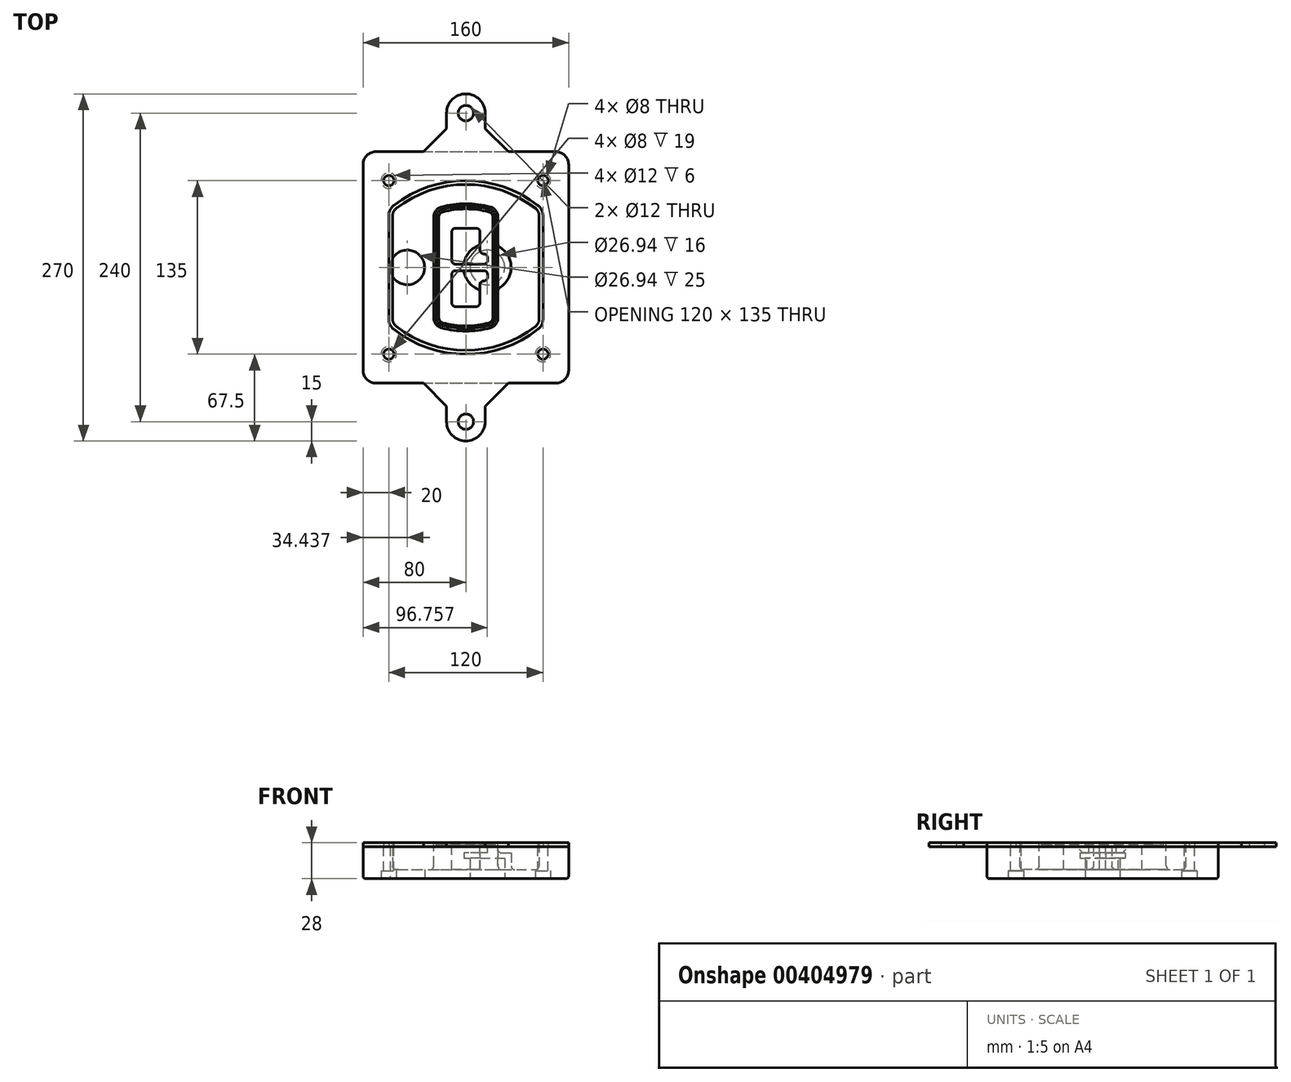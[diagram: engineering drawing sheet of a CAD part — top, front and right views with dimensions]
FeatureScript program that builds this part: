
annotation { "Feature Type Name" : "Feature", "Feature Type Description" : "" }
export const myFeature = defineFeature(function(context is Context, id is Id, definition is map)
    precondition{}
    {
        {
            var Q0;
            Q0=qCreatedBy(makeId("Top.planeOp"),FACE);
            var sketch = newSketch(context, id + "F0", { "sketchPlane" : qUnion([Q0])});
            skPoint(sketch, "E0.rect.middle", {"position": v(0, 0) * mm});
            skLineSegment(sketch, "E1.bottom", {"start": v(-70, -90) * mm, "end": v(70, -90) * mm});
            skLineSegment(sketch, "E1.top", {"start": v(-70, 90) * mm, "end": v(70, 90) * mm});
            skLineSegment(sketch, "E1.left", {"start": v(-80, -80) * mm, "end": v(-80, 80) * mm});
            skLineSegment(sketch, "E1.right", {"start": v(80, -80) * mm, "end": v(80, 80) * mm});
            skLineSegment(sketch, "E2", {"start": v(-80, 90) * mm, "end": v(80, -90) * mm, "construction": true});
            skLineSegment(sketch, "E3", {"start": v(80, 90) * mm, "end": v(-80, -90) * mm, "construction": true});
            skCircle(sketch, "E4", {"center": v(-60, 67.5) * mm, "radius": 4 * mm});
            skCircle(sketch, "E5", {"center": v(60, 67.5) * mm, "radius": 4 * mm});
            skCircle(sketch, "E6", {"center": v(60, -67.5) * mm, "radius": 4 * mm});
            skCircle(sketch, "E7", {"center": v(-60, -67.5) * mm, "radius": 4 * mm});
            skLineSegment(sketch, "E8", {"start": v(-60, 67.5) * mm, "end": v(60, 67.5) * mm, "construction": true});
            skLineSegment(sketch, "E9", {"start": v(60, 67.5) * mm, "end": v(60, -67.5) * mm, "construction": true});
            skLineSegment(sketch, "E10", {"start": v(60, -67.5) * mm, "end": v(-60, -67.5) * mm, "construction": true});
            skLineSegment(sketch, "E11", {"start": v(-60, -67.5) * mm, "end": v(-60, 67.5) * mm, "construction": true});
            skLineSegment(sketch, "E12", {"start": v(-60, 40.3) * mm, "end": v(-60, -40.3) * mm});
            skLineSegment(sketch, "E13", {"start": v(60, 40.3) * mm, "end": v(60, -40.3) * mm});
            skArc(sketch, "E14", {"start": v(56.15, 48.18) * mm, "mid": v(0, 67.5) * mm, "end": v(-56.15, 48.18) * mm});
            skArc(sketch, "E15", {"start": v(-56.15, -48.18) * mm, "mid": v(0, -67.5) * mm, "end": v(56.15, -48.18) * mm});
            skLineSegment(sketch, "E16", {"start": v(-60, 0) * mm, "end": v(60, 0) * mm, "construction": true});
            skPoint(sketch, "E17.visualSharp", {"position": v(-60, -45) * mm});
            skArc(sketch, "E17.filletArc", {"start": v(-60, -40.3) * mm, "mid": v(-58.99, -44.68) * mm, "end": v(-56.15, -48.18) * mm});
            skPoint(sketch, "E18.visualSharp", {"position": v(-60, 45) * mm});
            skArc(sketch, "E18.filletArc", {"start": v(-56.15, 48.18) * mm, "mid": v(-58.99, 44.68) * mm, "end": v(-60, 40.3) * mm});
            skPoint(sketch, "E19.visualSharp", {"position": v(60, 45) * mm});
            skArc(sketch, "E19.filletArc", {"start": v(60, 40.3) * mm, "mid": v(58.99, 44.68) * mm, "end": v(56.15, 48.18) * mm});
            skPoint(sketch, "E20.visualSharp", {"position": v(60, -45) * mm});
            skArc(sketch, "E20.filletArc", {"start": v(56.15, -48.18) * mm, "mid": v(58.99, -44.68) * mm, "end": v(60, -40.3) * mm});
            skPoint(sketch, "E21.visualSharp", {"position": v(-80, 90) * mm});
            skArc(sketch, "E21.filletArc", {"start": v(-70, 90) * mm, "mid": v(-77.07, 87.07) * mm, "end": v(-80, 80) * mm});
            skPoint(sketch, "E22.visualSharp", {"position": v(80, 90) * mm});
            skArc(sketch, "E22.filletArc", {"start": v(80, 80) * mm, "mid": v(77.07, 87.07) * mm, "end": v(70, 90) * mm});
            skPoint(sketch, "E23.visualSharp", {"position": v(80, -90) * mm});
            skArc(sketch, "E23.filletArc", {"start": v(70, -90) * mm, "mid": v(77.07, -87.07) * mm, "end": v(80, -80) * mm});
            skPoint(sketch, "E24.visualSharp", {"position": v(-80, -90) * mm});
            skArc(sketch, "E24.filletArc", {"start": v(-80, -80) * mm, "mid": v(-77.07, -87.07) * mm, "end": v(-70, -90) * mm});
            skArc(sketch, "E25.0", {"start": v(57, 40.3) * mm, "mid": v(56.3, 43.36) * mm, "end": v(54.3, 45.81) * mm});
            skLineSegment(sketch, "E25.1", {"start": v(57, 40.3) * mm, "end": v(57, -40.3) * mm});
            skArc(sketch, "E25.2", {"start": v(54.3, -45.81) * mm, "mid": v(56.3, -43.36) * mm, "end": v(57, -40.3) * mm});
            skArc(sketch, "E25.3", {"start": v(-54.3, -45.81) * mm, "mid": v(0, -64.5) * mm, "end": v(54.3, -45.81) * mm});
            skArc(sketch, "E25.4", {"start": v(-57, -40.3) * mm, "mid": v(-56.3, -43.36) * mm, "end": v(-54.3, -45.81) * mm});
            skArc(sketch, "E25.5", {"start": v(54.3, 45.81) * mm, "mid": v(0, 64.5) * mm, "end": v(-54.3, 45.81) * mm});
            skLineSegment(sketch, "E25.6", {"start": v(-57, 40.3) * mm, "end": v(-57, -40.3) * mm});
            skArc(sketch, "E25.7", {"start": v(-54.3, 45.81) * mm, "mid": v(-56.3, 43.36) * mm, "end": v(-57, 40.3) * mm});
            skArc(sketch, "E26.0", {"start": v(-58.62, 51.33) * mm, "mid": v(-62.58, 46.43) * mm, "end": v(-64, 40.3) * mm});
            skArc(sketch, "E26.1", {"start": v(58.62, 51.33) * mm, "mid": v(0, 71.5) * mm, "end": v(-58.62, 51.33) * mm});
            skArc(sketch, "E26.2", {"start": v(64, 40.3) * mm, "mid": v(62.58, 46.43) * mm, "end": v(58.62, 51.33) * mm});
            skLineSegment(sketch, "E26.3", {"start": v(64, 40.3) * mm, "end": v(64, -40.3) * mm});
            skArc(sketch, "E26.4", {"start": v(58.62, -51.33) * mm, "mid": v(62.58, -46.43) * mm, "end": v(64, -40.3) * mm});
            skLineSegment(sketch, "E26.5", {"start": v(-64, 40.3) * mm, "end": v(-64, -40.3) * mm});
            skArc(sketch, "E26.6", {"start": v(-58.62, -51.33) * mm, "mid": v(0, -71.5) * mm, "end": v(58.62, -51.33) * mm});
            skArc(sketch, "E26.7", {"start": v(-64, -40.3) * mm, "mid": v(-62.58, -46.43) * mm, "end": v(-58.62, -51.33) * mm});
            skSolve(sketch);
        }
        {
            var Q0;
            Q0=makeQuery(id+"F0.imprint","IMPRINT",FACE,{"disambiguationData":[TD([[makeQuery(id+"F0.imprint","IMPRINT",EDGE,{"derivedFrom":sQuery(id+"F0.wireOp",EDGE,"E1.bottom")}),1.0]])]});
            var Q1;
            Q1=makeQuery(id+"F0.imprint","IMPRINT",FACE,{"disambiguationData":[TD([[makeQuery(id+"F0.imprint","IMPRINT",EDGE,{"derivedFrom":sQuery(id+"F0.wireOp",EDGE,"E12")}),1.0]])]});
            var Q2;
            Q2=makeQuery(id+"F0.imprint","IMPRINT",FACE,{"disambiguationData":[TD([[makeQuery(id+"F0.imprint","IMPRINT",EDGE,{"derivedFrom":sQuery(id+"F0.wireOp",EDGE,"E25.0")}),1.0]])]});
            var Q3;
            Q3=makeQuery(id+"F0.imprint","IMPRINT",FACE,{"disambiguationData":[TD([[makeQuery(id+"F0.imprint","IMPRINT",EDGE,{"derivedFrom":sQuery(id+"F0.wireOp",EDGE,"E12")}),-1.0]])]});
            extrude(context, id + "F1", {"entities" : qUnion([Q0, Q1, Q2, Q3]), "oppositeDirection" : true, "depth" : 25 * mm});
        }
        {
            var Q0;
            Q0=makeQuery(id+"F0.imprint","IMPRINT",FACE,{"disambiguationData":[TD([[makeQuery(id+"F0.imprint","IMPRINT",EDGE,{"derivedFrom":sQuery(id+"F0.wireOp",EDGE,"E12")}),1.0]])]});
            extrude(context, id + "F2", {"entities" : qUnion([Q0]), "operationType" : NewBodyOperationType.ADD, "depth" : 3 * mm});
        }
        {
            var Q0;
            Q0=makeQuery(id+"F0.imprint","IMPRINT",FACE,{"disambiguationData":[TD([[makeQuery(id+"F0.imprint","IMPRINT",EDGE,{"derivedFrom":sQuery(id+"F0.wireOp",EDGE,"E25.0")}),1.0]])]});
            extrude(context, id + "F3", {"entities" : qUnion([Q0]), "operationType" : NewBodyOperationType.REMOVE, "oppositeDirection" : true, "depth" : 18 * mm});
        }
        {
            var Q0;
            Q0=makeQuery(id+"F2.opExtrude","CAP_FACE",FACE,{"disambiguationData":[OSD([sQuery(id+"F0.wireOp",EDGE,"E12"),sQuery(id+"F0.wireOp",EDGE,"E13"),sQuery(id+"F0.wireOp",EDGE,"E14"),sQuery(id+"F0.wireOp",EDGE,"E15"),sQuery(id+"F0.wireOp",EDGE,"E17.filletArc"),sQuery(id+"F0.wireOp",EDGE,"E18.filletArc"),sQuery(id+"F0.wireOp",EDGE,"E19.filletArc"),sQuery(id+"F0.wireOp",EDGE,"E20.filletArc"),sQuery(id+"F0.wireOp",EDGE,"E25.0"),sQuery(id+"F0.wireOp",EDGE,"E25.1"),sQuery(id+"F0.wireOp",EDGE,"E25.2"),sQuery(id+"F0.wireOp",EDGE,"E25.3"),sQuery(id+"F0.wireOp",EDGE,"E25.4"),sQuery(id+"F0.wireOp",EDGE,"E25.5"),sQuery(id+"F0.wireOp",EDGE,"E25.6"),sQuery(id+"F0.wireOp",EDGE,"E25.7")])],"isStart":false});
            var sketch = newSketch(context, id + "F4", { "sketchPlane" : qUnion([Q0])});
            skArc(sketch, "E27.0", {"start": v(-19.08, -46.97) * mm, "mid": v(0, -49.5) * mm, "end": v(19.08, -46.97) * mm});
            skArc(sketch, "E28.0", {"start": v(19.08, 46.97) * mm, "mid": v(0, 49.5) * mm, "end": v(-19.08, 46.97) * mm});
            skLineSegment(sketch, "E29", {"start": v(-25, 39.25) * mm, "end": v(-25, -39.25) * mm});
            skLineSegment(sketch, "E30", {"start": v(25, 39.25) * mm, "end": v(25, -39.25) * mm});
            skLineSegment(sketch, "E31", {"start": v(-25, 45.1) * mm, "end": v(25, 45.1) * mm, "construction": true});
            skLineSegment(sketch, "E32", {"start": v(-25, -45.1) * mm, "end": v(25, -45.1) * mm, "construction": true});
            skPoint(sketch, "E33.visualSharp", {"position": v(-25, 45.1) * mm});
            skArc(sketch, "E33.filletArc", {"start": v(-19.08, 46.97) * mm, "mid": v(-23.35, 44.11) * mm, "end": v(-25, 39.25) * mm});
            skPoint(sketch, "E34.visualSharp", {"position": v(25, 45.1) * mm});
            skArc(sketch, "E34.filletArc", {"start": v(25, 39.25) * mm, "mid": v(23.35, 44.11) * mm, "end": v(19.08, 46.97) * mm});
            skPoint(sketch, "E35.visualSharp", {"position": v(25, -45.1) * mm});
            skArc(sketch, "E35.filletArc", {"start": v(19.08, -46.97) * mm, "mid": v(23.35, -44.11) * mm, "end": v(25, -39.25) * mm});
            skPoint(sketch, "E36.visualSharp", {"position": v(-25, -45.1) * mm});
            skArc(sketch, "E36.filletArc", {"start": v(-25, -39.25) * mm, "mid": v(-23.35, -44.11) * mm, "end": v(-19.08, -46.97) * mm});
            skArc(sketch, "E37.0", {"start": v(54.3, 45.81) * mm, "mid": v(0, 64.5) * mm, "end": v(-54.3, 45.81) * mm});
            skArc(sketch, "E37.1", {"start": v(-54.3, 45.81) * mm, "mid": v(-56.3, 43.36) * mm, "end": v(-57, 40.3) * mm});
            skLineSegment(sketch, "E37.2", {"start": v(-57, 40.3) * mm, "end": v(-57, -40.3) * mm});
            skArc(sketch, "E37.3", {"start": v(-57, -40.3) * mm, "mid": v(-56.3, -43.36) * mm, "end": v(-54.3, -45.81) * mm});
            skArc(sketch, "E37.4", {"start": v(-54.3, -45.81) * mm, "mid": v(0, -64.5) * mm, "end": v(54.3, -45.81) * mm});
            skArc(sketch, "E37.5", {"start": v(54.3, -45.81) * mm, "mid": v(56.3, -43.36) * mm, "end": v(57, -40.3) * mm});
            skLineSegment(sketch, "E37.6", {"start": v(57, 40.3) * mm, "end": v(57, -40.3) * mm});
            skArc(sketch, "E37.7", {"start": v(57, 40.3) * mm, "mid": v(56.3, 43.36) * mm, "end": v(54.3, 45.81) * mm});
            skLineSegment(sketch, "E38.0", {"start": v(23, 39.25) * mm, "end": v(23, -39.25) * mm});
            skArc(sketch, "E38.1", {"start": v(18.56, -45.04) * mm, "mid": v(21.76, -42.9) * mm, "end": v(23, -39.25) * mm});
            skArc(sketch, "E38.2", {"start": v(-18.56, -45.04) * mm, "mid": v(0, -47.5) * mm, "end": v(18.56, -45.04) * mm});
            skArc(sketch, "E38.3", {"start": v(-23, -39.25) * mm, "mid": v(-21.76, -42.9) * mm, "end": v(-18.56, -45.04) * mm});
            skLineSegment(sketch, "E38.4", {"start": v(-23, 39.25) * mm, "end": v(-23, -39.25) * mm});
            skArc(sketch, "E38.5", {"start": v(23, 39.25) * mm, "mid": v(21.76, 42.9) * mm, "end": v(18.56, 45.04) * mm});
            skArc(sketch, "E38.6", {"start": v(-18.56, 45.04) * mm, "mid": v(-21.76, 42.9) * mm, "end": v(-23, 39.25) * mm});
            skArc(sketch, "E38.7", {"start": v(18.56, 45.04) * mm, "mid": v(0, 47.5) * mm, "end": v(-18.56, 45.04) * mm});
            skArc(sketch, "E39.0", {"start": v(21, 39.25) * mm, "mid": v(20.18, 41.68) * mm, "end": v(18.04, 43.1) * mm});
            skLineSegment(sketch, "E39.1", {"start": v(21, 39.25) * mm, "end": v(21, -39.25) * mm});
            skArc(sketch, "E39.2", {"start": v(18.04, -43.1) * mm, "mid": v(20.18, -41.68) * mm, "end": v(21, -39.25) * mm});
            skArc(sketch, "E39.3", {"start": v(-18.04, -43.1) * mm, "mid": v(0, -45.5) * mm, "end": v(18.04, -43.1) * mm});
            skArc(sketch, "E39.4", {"start": v(-21, -39.25) * mm, "mid": v(-20.18, -41.68) * mm, "end": v(-18.04, -43.1) * mm});
            skArc(sketch, "E39.5", {"start": v(18.04, 43.1) * mm, "mid": v(0, 45.5) * mm, "end": v(-18.04, 43.1) * mm});
            skLineSegment(sketch, "E39.6", {"start": v(-21, 39.25) * mm, "end": v(-21, -39.25) * mm});
            skArc(sketch, "E39.7", {"start": v(-18.04, 43.1) * mm, "mid": v(-20.18, 41.68) * mm, "end": v(-21, 39.25) * mm});
            skLineSegment(sketch, "E40", {"start": v(-25, 0) * mm, "end": v(25, 0) * mm, "construction": true});
            skLineSegment(sketch, "E41", {"start": v(-11, 5.5) * mm, "end": v(-11, 27.5) * mm});
            skLineSegment(sketch, "E42", {"start": v(-8, 30.5) * mm, "end": v(8, 30.5) * mm});
            skLineSegment(sketch, "E43", {"start": v(11, 27.5) * mm, "end": v(11, 13.5) * mm});
            skLineSegment(sketch, "E44", {"start": v(14, 10.5) * mm, "end": v(14, 10.5) * mm});
            skLineSegment(sketch, "E45", {"start": v(17, 7.5) * mm, "end": v(17, 5.5) * mm});
            skLineSegment(sketch, "E46", {"start": v(14, 2.5) * mm, "end": v(-8, 2.5) * mm});
            skPoint(sketch, "E47.visualSharp", {"position": v(-11, 30.5) * mm});
            skArc(sketch, "E47.filletArc", {"start": v(-8, 30.5) * mm, "mid": v(-10.12, 29.62) * mm, "end": v(-11, 27.5) * mm});
            skPoint(sketch, "E48.visualSharp", {"position": v(11, 30.5) * mm});
            skArc(sketch, "E48.filletArc", {"start": v(11, 27.5) * mm, "mid": v(10.12, 29.62) * mm, "end": v(8, 30.5) * mm});
            skPoint(sketch, "E49.visualSharp", {"position": v(11, 10.5) * mm});
            skArc(sketch, "E49.filletArc", {"start": v(11, 13.5) * mm, "mid": v(11.88, 11.38) * mm, "end": v(14, 10.5) * mm});
            skPoint(sketch, "E50.visualSharp", {"position": v(17, 10.5) * mm});
            skArc(sketch, "E50.filletArc", {"start": v(17, 7.5) * mm, "mid": v(16.12, 9.62) * mm, "end": v(14, 10.5) * mm});
            skPoint(sketch, "E51.visualSharp", {"position": v(17, 2.5) * mm});
            skArc(sketch, "E51.filletArc", {"start": v(14, 2.5) * mm, "mid": v(16.12, 3.38) * mm, "end": v(17, 5.5) * mm});
            skPoint(sketch, "E52.visualSharp", {"position": v(-11, 2.5) * mm});
            skArc(sketch, "E52.filletArc", {"start": v(-11, 5.5) * mm, "mid": v(-10.12, 3.38) * mm, "end": v(-8, 2.5) * mm});
            skLineSegment(sketch, "E53.0.MirrorCS", {"start": v(14, -2.5) * mm, "end": v(-8, -2.5) * mm});
            skArc(sketch, "E54.0.MirrorCS", {"start": v(-11, -5.5) * mm, "mid": v(-10.12, -3.38) * mm, "end": v(-8, -2.5) * mm});
            skLineSegment(sketch, "E55.0.MirrorCS", {"start": v(-11, -5.5) * mm, "end": v(-11, -27.5) * mm});
            skArc(sketch, "E56.0.MirrorCS", {"start": v(-8, -30.5) * mm, "mid": v(-10.12, -29.62) * mm, "end": v(-11, -27.5) * mm});
            skLineSegment(sketch, "E57.0.MirrorCS", {"start": v(-8, -30.5) * mm, "end": v(8, -30.5) * mm});
            skArc(sketch, "E58.0.MirrorCS", {"start": v(11, -27.5) * mm, "mid": v(10.12, -29.62) * mm, "end": v(8, -30.5) * mm});
            skLineSegment(sketch, "E59.0.MirrorCS", {"start": v(11, -27.5) * mm, "end": v(11, -13.5) * mm});
            skArc(sketch, "E60.0.MirrorCS", {"start": v(11, -13.5) * mm, "mid": v(11.88, -11.38) * mm, "end": v(14, -10.5) * mm});
            skArc(sketch, "E61.0.MirrorCS", {"start": v(17, -7.5) * mm, "mid": v(16.12, -9.62) * mm, "end": v(14, -10.5) * mm});
            skLineSegment(sketch, "E62.0.MirrorCS", {"start": v(17, -7.5) * mm, "end": v(17, -5.5) * mm});
            skArc(sketch, "E63.0.MirrorCS", {"start": v(14, -2.5) * mm, "mid": v(16.12, -3.38) * mm, "end": v(17, -5.5) * mm});
            skSolve(sketch);
        }
        {
            var Q0;
            Q0=makeQuery(id+"F4.imprint","IMPRINT",FACE,{"disambiguationData":[TD([[makeQuery(id+"F4.imprint","IMPRINT",EDGE,{"derivedFrom":sQuery(id+"F4.wireOp",EDGE,"E27.0")}),1.0]])]});
            var Q1;
            Q1=makeQuery(id+"F4.imprint","IMPRINT",FACE,{"disambiguationData":[TD([[makeQuery(id+"F4.imprint","IMPRINT",EDGE,{"derivedFrom":sQuery(id+"F4.wireOp",EDGE,"E38.0")}),-1.0]])]});
            var Q2;
            Q2=makeQuery(id+"F4.imprint","IMPRINT",FACE,{"disambiguationData":[TD([[makeQuery(id+"F4.imprint","IMPRINT",EDGE,{"derivedFrom":sQuery(id+"F4.wireOp",EDGE,"E39.0")}),1.0]])]});
            extrude(context, id + "F5", {"entities" : qUnion([Q0, Q1, Q2]), "operationType" : NewBodyOperationType.ADD, "endBound" : BoundingType.UP_TO_NEXT, "oppositeDirection" : true, "depth" : 25 * mm});
        }
        {
            var Q0;
            Q0=makeQuery(id+"F4.imprint","IMPRINT",FACE,{"disambiguationData":[TD([[makeQuery(id+"F4.imprint","IMPRINT",EDGE,{"derivedFrom":sQuery(id+"F4.wireOp",EDGE,"E38.0")}),-1.0]])]});
            extrude(context, id + "F6", {"entities" : qUnion([Q0]), "operationType" : NewBodyOperationType.REMOVE, "oppositeDirection" : true, "depth" : 2 * mm});
        }
        {
            var Q0;
            Q0=makeQuery(id+"F1.opExtrude","CAP_FACE",FACE,{"disambiguationData":[OSD([sQuery(id+"F0.wireOp",EDGE,"E1.bottom"),sQuery(id+"F0.wireOp",EDGE,"E1.top"),sQuery(id+"F0.wireOp",EDGE,"E1.left"),sQuery(id+"F0.wireOp",EDGE,"E1.right"),sQuery(id+"F0.wireOp",EDGE,"E4"),sQuery(id+"F0.wireOp",EDGE,"E5"),sQuery(id+"F0.wireOp",EDGE,"E6"),sQuery(id+"F0.wireOp",EDGE,"E7"),sQuery(id+"F0.wireOp",EDGE,"E21.filletArc"),sQuery(id+"F0.wireOp",EDGE,"E22.filletArc"),sQuery(id+"F0.wireOp",EDGE,"E23.filletArc"),sQuery(id+"F0.wireOp",EDGE,"E24.filletArc")])],"isStart":false});
            var sketch = newSketch(context, id + "F7", { "sketchPlane" : qUnion([Q0])});
            skCircle(sketch, "E64", {"center": v(16.76, 0) * mm, "radius": 13.47 * mm});
            skCircle(sketch, "E65", {"center": v(-45.56, 0) * mm, "radius": 13.47 * mm});
            skLineSegment(sketch, "E66", {"start": v(80, 0) * mm, "end": v(-80, 0) * mm});
            skCircle(sketch, "E67", {"center": v(16.76, 0) * mm, "radius": 18.47 * mm});
            skCircle(sketch, "E68", {"center": v(60, -67.5) * mm, "radius": 6 * mm});
            skCircle(sketch, "E69", {"center": v(-60, -67.5) * mm, "radius": 6 * mm});
            skCircle(sketch, "E70", {"center": v(-60, 67.5) * mm, "radius": 6 * mm});
            skCircle(sketch, "E71", {"center": v(60, 67.5) * mm, "radius": 6 * mm});
            skSolve(sketch);
        }
        {
            var Q0;
            {var subQ1=sQuery(id+"F7.wireOp",EDGE,"E66");var subQ4=sQuery(id+"F7.wireOp",EDGE,"E64");var subQ6=makeQuery(id+"F7.imprint","INTERSECT",VERTEX,{"disambiguationData":[OD(0.0)],"derivedFrom":[subQ4,subQ1]});Q0=makeQuery(id+"F7.imprint","IMPRINT",FACE,{"disambiguationData":[TD([[makeQuery(id+"F7.imprint","IMPRINT",EDGE,{"disambiguationData":[TD([[subQ6,-1.0]])],"derivedFrom":subQ4}),-1.0]])]});}
            var Q1;
            {var subQ0=sQuery(id+"F7.wireOp",EDGE,"E66");var subQ1=sQuery(id+"F7.wireOp",EDGE,"E64");var subQ3=makeQuery(id+"F7.imprint","INTERSECT",VERTEX,{"disambiguationData":[OD(0.0)],"derivedFrom":[subQ1,subQ0]});Q1=makeQuery(id+"F7.imprint","IMPRINT",FACE,{"disambiguationData":[TD([[makeQuery(id+"F7.imprint","IMPRINT",EDGE,{"disambiguationData":[TD([[subQ3,-1.0]])],"derivedFrom":subQ1}),1.0]])]});}
            var Q2;
            {var subQ0=sQuery(id+"F7.wireOp",EDGE,"E66");var subQ1=sQuery(id+"F7.wireOp",EDGE,"E64");var subQ3=makeQuery(id+"F7.imprint","INTERSECT",VERTEX,{"disambiguationData":[OD(0.0)],"derivedFrom":[subQ1,subQ0]});Q2=makeQuery(id+"F7.imprint","IMPRINT",FACE,{"disambiguationData":[TD([[makeQuery(id+"F7.imprint","IMPRINT",EDGE,{"disambiguationData":[TD([[subQ3,1.0]])],"derivedFrom":subQ1}),1.0]])]});}
            var Q3;
            {var subQ1=sQuery(id+"F7.wireOp",EDGE,"E66");var subQ4=sQuery(id+"F7.wireOp",EDGE,"E64");var subQ6=makeQuery(id+"F7.imprint","INTERSECT",VERTEX,{"disambiguationData":[OD(0.0)],"derivedFrom":[subQ4,subQ1]});Q3=makeQuery(id+"F7.imprint","IMPRINT",FACE,{"disambiguationData":[TD([[makeQuery(id+"F7.imprint","IMPRINT",EDGE,{"disambiguationData":[TD([[subQ6,1.0]])],"derivedFrom":subQ4}),-1.0]])]});}
            extrude(context, id + "F8", {"entities" : qUnion([Q0, Q1, Q2, Q3]), "operationType" : NewBodyOperationType.ADD, "oppositeDirection" : true, "depth" : 20 * mm});
        }
        {
            var Q0;
            {var subQ0=sQuery(id+"F7.wireOp",EDGE,"E66");var subQ1=sQuery(id+"F7.wireOp",EDGE,"E64");var subQ3=makeQuery(id+"F7.imprint","INTERSECT",VERTEX,{"disambiguationData":[OD(0.0)],"derivedFrom":[subQ1,subQ0]});Q0=makeQuery(id+"F7.imprint","IMPRINT",FACE,{"disambiguationData":[TD([[makeQuery(id+"F7.imprint","IMPRINT",EDGE,{"disambiguationData":[TD([[subQ3,-1.0]])],"derivedFrom":subQ1}),1.0]])]});}
            var Q1;
            {var subQ0=sQuery(id+"F7.wireOp",EDGE,"E66");var subQ1=sQuery(id+"F7.wireOp",EDGE,"E64");var subQ3=makeQuery(id+"F7.imprint","INTERSECT",VERTEX,{"disambiguationData":[OD(0.0)],"derivedFrom":[subQ1,subQ0]});Q1=makeQuery(id+"F7.imprint","IMPRINT",FACE,{"disambiguationData":[TD([[makeQuery(id+"F7.imprint","IMPRINT",EDGE,{"disambiguationData":[TD([[subQ3,1.0]])],"derivedFrom":subQ1}),1.0]])]});}
            extrude(context, id + "F9", {"entities" : qUnion([Q0, Q1]), "operationType" : NewBodyOperationType.REMOVE, "oppositeDirection" : true, "depth" : 16 * mm});
        }
        {
            var Q0;
            {var subQ0=sQuery(id+"F7.wireOp",EDGE,"E66");var subQ1=sQuery(id+"F7.wireOp",EDGE,"E65");var subQ3=makeQuery(id+"F7.imprint","INTERSECT",VERTEX,{"disambiguationData":[OD(0.0)],"derivedFrom":[subQ1,subQ0]});Q0=makeQuery(id+"F7.imprint","IMPRINT",FACE,{"disambiguationData":[TD([[makeQuery(id+"F7.imprint","IMPRINT",EDGE,{"disambiguationData":[TD([[subQ3,-1.0]])],"derivedFrom":subQ1}),1.0]])]});}
            var Q1;
            {var subQ0=sQuery(id+"F7.wireOp",EDGE,"E66");var subQ1=sQuery(id+"F7.wireOp",EDGE,"E65");var subQ3=makeQuery(id+"F7.imprint","INTERSECT",VERTEX,{"disambiguationData":[OD(0.0)],"derivedFrom":[subQ1,subQ0]});Q1=makeQuery(id+"F7.imprint","IMPRINT",FACE,{"disambiguationData":[TD([[makeQuery(id+"F7.imprint","IMPRINT",EDGE,{"disambiguationData":[TD([[subQ3,1.0]])],"derivedFrom":subQ1}),1.0]])]});}
            extrude(context, id + "F10", {"entities" : qUnion([Q0, Q1]), "operationType" : NewBodyOperationType.REMOVE, "oppositeDirection" : true, "depth" : 25 * mm});
        }
        {
            var Q0;
            Q0=makeQuery(id+"F7.imprint","IMPRINT",FACE,{"disambiguationData":[TD([[makeQuery(id+"F7.imprint","IMPRINT",EDGE,{"derivedFrom":sQuery(id+"F7.wireOp",EDGE,"E68")}),1.0]])]});
            var Q1;
            Q1=makeQuery(id+"F7.imprint","IMPRINT",FACE,{"disambiguationData":[TD([[makeQuery(id+"F7.imprint","IMPRINT",EDGE,{"derivedFrom":makeQuery(id+"F1.opExtrude","CAP_EDGE",EDGE,{"disambiguationData":[OSD([sQuery(id+"F0.wireOp",EDGE,"E5")])],"isStart":false})}),-1.0]])]});
            var Q2;
            Q2=makeQuery(id+"F7.imprint","IMPRINT",FACE,{"disambiguationData":[TD([[makeQuery(id+"F7.imprint","IMPRINT",EDGE,{"derivedFrom":sQuery(id+"F7.wireOp",EDGE,"E69")}),1.0]])]});
            var Q3;
            Q3=makeQuery(id+"F7.imprint","IMPRINT",FACE,{"disambiguationData":[TD([[makeQuery(id+"F7.imprint","IMPRINT",EDGE,{"derivedFrom":makeQuery(id+"F1.opExtrude","CAP_EDGE",EDGE,{"disambiguationData":[OSD([sQuery(id+"F0.wireOp",EDGE,"E4")])],"isStart":false})}),-1.0]])]});
            var Q4;
            Q4=makeQuery(id+"F7.imprint","IMPRINT",FACE,{"disambiguationData":[TD([[makeQuery(id+"F7.imprint","IMPRINT",EDGE,{"derivedFrom":sQuery(id+"F7.wireOp",EDGE,"E70")}),1.0]])]});
            var Q5;
            Q5=makeQuery(id+"F7.imprint","IMPRINT",FACE,{"disambiguationData":[TD([[makeQuery(id+"F7.imprint","IMPRINT",EDGE,{"derivedFrom":makeQuery(id+"F1.opExtrude","CAP_EDGE",EDGE,{"disambiguationData":[OSD([sQuery(id+"F0.wireOp",EDGE,"E7")])],"isStart":false})}),-1.0]])]});
            var Q6;
            Q6=makeQuery(id+"F7.imprint","IMPRINT",FACE,{"disambiguationData":[TD([[makeQuery(id+"F7.imprint","IMPRINT",EDGE,{"derivedFrom":sQuery(id+"F7.wireOp",EDGE,"E71")}),1.0]])]});
            var Q7;
            Q7=makeQuery(id+"F7.imprint","IMPRINT",FACE,{"disambiguationData":[TD([[makeQuery(id+"F7.imprint","IMPRINT",EDGE,{"derivedFrom":makeQuery(id+"F1.opExtrude","CAP_EDGE",EDGE,{"disambiguationData":[OSD([sQuery(id+"F0.wireOp",EDGE,"E6")])],"isStart":false})}),-1.0]])]});
            extrude(context, id + "F11", {"entities" : qUnion([Q0, Q1, Q2, Q3, Q4, Q5, Q6, Q7]), "operationType" : NewBodyOperationType.REMOVE, "oppositeDirection" : true, "depth" : 6 * mm});
        }
        {
            var Q0;
            Q0=makeQuery(id+"F9.boolean.opBoolean","COPY",FACE,{"derivedFrom":makeQuery(id+"F9.opExtrude","CAP_FACE",FACE,{"disambiguationData":[OSD([sQuery(id+"F7.wireOp",EDGE,"E64")])],"isStart":false})});
            var sketch = newSketch(context, id + "F12", { "sketchPlane" : qUnion([Q0])});
            skArc(sketch, "E72.0", {"start": v(11, 17.55) * mm, "mid": v(2.57, 11.82) * mm, "end": v(-1.54, 2.5) * mm});
            skArc(sketch, "E72.1", {"start": v(-1.54, -2.5) * mm, "mid": v(2.57, -11.82) * mm, "end": v(11, -17.55) * mm});
            skLineSegment(sketch, "E73", {"start": v(-1.54, -2.5) * mm, "end": v(14, -2.5) * mm});
            skLineSegment(sketch, "E74.0", {"start": v(14, 2.5) * mm, "end": v(-1.54, 2.5) * mm});
            skArc(sketch, "E74.1", {"start": v(14, 2.5) * mm, "mid": v(16.12, 3.38) * mm, "end": v(17, 5.5) * mm});
            skLineSegment(sketch, "E74.2", {"start": v(17, 7.5) * mm, "end": v(17, 5.5) * mm});
            skArc(sketch, "E74.3", {"start": v(17, 7.5) * mm, "mid": v(16.12, 9.62) * mm, "end": v(14, 10.5) * mm});
            skArc(sketch, "E74.4", {"start": v(11, 13.5) * mm, "mid": v(11.88, 11.38) * mm, "end": v(14, 10.5) * mm});
            skLineSegment(sketch, "E74.5", {"start": v(11, 17.55) * mm, "end": v(11, 13.5) * mm});
            skLineSegment(sketch, "E74.7", {"start": v(14, -2.5) * mm, "end": v(-1.54, -2.5) * mm});
            skArc(sketch, "E74.8", {"start": v(14, -2.5) * mm, "mid": v(16.12, -3.38) * mm, "end": v(17, -5.5) * mm});
            skLineSegment(sketch, "E74.9", {"start": v(17, -7.5) * mm, "end": v(17, -5.5) * mm});
            skArc(sketch, "E74.10", {"start": v(17, -7.5) * mm, "mid": v(16.12, -9.62) * mm, "end": v(14, -10.5) * mm});
            skArc(sketch, "E74.11", {"start": v(11, -13.5) * mm, "mid": v(11.88, -11.38) * mm, "end": v(14, -10.5) * mm});
            skLineSegment(sketch, "E74.12", {"start": v(11, -17.55) * mm, "end": v(11, -13.5) * mm});
            skPoint(sketch, "E75.orphan", {"position": v(11, -27.5) * mm});
            skPoint(sketch, "E76.orphan", {"position": v(-8, -2.5) * mm});
            skPoint(sketch, "E77.orphan", {"position": v(-8, 2.5) * mm});
            skPoint(sketch, "E78.orphan", {"position": v(11, 27.5) * mm});
            skSolve(sketch);
        }
        {
            var Q0;
            {var subQ7=sQuery(id+"F12.wireOp",EDGE,"E72.0");var subQ14=sQuery(id+"F12.wireOp",EDGE,"E72.1");var subQ16=sQuery(id+"F12.wireOp",EDGE,"E74.1");var subQ18=sQuery(id+"F12.wireOp",EDGE,"E74.8");Q0=qUnion([makeQuery(id+"F12.imprint","IMPRINT",FACE,{"disambiguationData":[TD([[makeQuery(id+"F12.imprint","IMPRINT",EDGE,{"derivedFrom":subQ7}),1.0]])]}),makeQuery(id+"F12.imprint","IMPRINT",FACE,{"disambiguationData":[TD([[makeQuery(id+"F12.imprint","IMPRINT",EDGE,{"derivedFrom":subQ14}),1.0]])]}),makeQuery(id+"F12.imprint","IMPRINT",FACE,{"disambiguationData":[TD([[makeQuery(id+"F12.imprint","IMPRINT",EDGE,{"derivedFrom":subQ16}),1.0]])]}),makeQuery(id+"F12.imprint","IMPRINT",FACE,{"disambiguationData":[TD([[makeQuery(id+"F12.imprint","IMPRINT",EDGE,{"derivedFrom":subQ18}),-1.0]])]})]);}
            var Q1;
            Q1=makeQuery(id+"F5.boolean.opBoolean","SPLIT",FACE,{"disambiguationData":[TD([makeQuery(id+"F5.opExtrude","SWEPT_FACE",FACE,{"disambiguationData":[OSD([sQuery(id+"F4.wireOp",EDGE,"E41")])]})])],"derivedFrom":makeQuery(id+"F3.boolean.opBoolean","COPY",FACE,{"derivedFrom":makeQuery(id+"F3.opExtrude","CAP_FACE",FACE,{"disambiguationData":[OSD([sQuery(id+"F0.wireOp",EDGE,"E25.0"),sQuery(id+"F0.wireOp",EDGE,"E25.1"),sQuery(id+"F0.wireOp",EDGE,"E25.2"),sQuery(id+"F0.wireOp",EDGE,"E25.3"),sQuery(id+"F0.wireOp",EDGE,"E25.4"),sQuery(id+"F0.wireOp",EDGE,"E25.5"),sQuery(id+"F0.wireOp",EDGE,"E25.6"),sQuery(id+"F0.wireOp",EDGE,"E25.7")])],"isStart":false})})});
            extrude(context, id + "F13", {"entities" : qUnion([Q0]), "operationType" : NewBodyOperationType.REMOVE, "endBound" : BoundingType.UP_TO_SURFACE, "endBoundEntityFace" : qUnion([Q1]), "depth" : 25 * mm});
        }
        {
            var Q0;
            Q0=makeQuery(id+"F3.boolean.opBoolean","COPY",EDGE,{"derivedFrom":makeQuery(id+"F3.opExtrude","CAP_EDGE",EDGE,{"disambiguationData":[OSD([sQuery(id+"F0.wireOp",EDGE,"E25.6")])],"isStart":false})});
            var Q1;
            Q1=makeQuery(id+"F8.boolean.opBoolean","INTERSECT",EDGE,{"derivedFrom":[makeQuery(id+"F5.opExtrude","SWEPT_FACE",FACE,{"disambiguationData":[OSD([sQuery(id+"F4.wireOp",EDGE,"E30")])]}),makeQuery(id+"F8.opExtrude","CAP_FACE",FACE,{"disambiguationData":[OSD([sQuery(id+"F7.wireOp",EDGE,"E67")])],"isStart":false})]});
            var Q2;
            Q2=makeQuery(id+"F8.boolean.opBoolean","INTERSECT",EDGE,{"disambiguationData":[OD(1.0)],"derivedFrom":[makeQuery(id+"F5.opExtrude","SWEPT_FACE",FACE,{"disambiguationData":[OSD([sQuery(id+"F4.wireOp",EDGE,"E30")])]}),makeQuery(id+"F8.opExtrude","SWEPT_FACE",FACE,{"disambiguationData":[OSD([sQuery(id+"F7.wireOp",EDGE,"E67")])]})]});
            var Q3;
            {var subQ0=sQuery(id+"F4.wireOp",EDGE,"E30");Q3=makeQuery(id+"F8.boolean.opBoolean","SPLIT",EDGE,{"disambiguationData":[TD([makeQuery(id+"F5.opExtrude","SWEPT_FACE",FACE,{"disambiguationData":[OSD([sQuery(id+"F4.wireOp",EDGE,"E35.filletArc")])]})])],"derivedFrom":makeQuery(id+"F5.opExtrude","CAP_EDGE",EDGE,{"disambiguationData":[OSD([subQ0])],"isStart":false})});}
            var Q4;
            {var subQ0=sQuery(id+"F0.wireOp",EDGE,"E25.7");var subQ1=sQuery(id+"F0.wireOp",EDGE,"E25.1");var subQ2=sQuery(id+"F0.wireOp",EDGE,"E25.6");var subQ3=sQuery(id+"F0.wireOp",EDGE,"E25.5");var subQ4=sQuery(id+"F0.wireOp",EDGE,"E25.4");var subQ5=sQuery(id+"F0.wireOp",EDGE,"E25.0");var subQ6=sQuery(id+"F0.wireOp",EDGE,"E25.2");var subQ7=sQuery(id+"F0.wireOp",EDGE,"E25.3");Q4=makeQuery(id+"F8.boolean.opBoolean","INTERSECT",EDGE,{"derivedFrom":[makeQuery(id+"F5.boolean.opBoolean","SPLIT",FACE,{"disambiguationData":[TD([makeQuery(id+"F2.opExtrude","SWEPT_FACE",FACE,{"disambiguationData":[OSD([subQ5])]})])],"derivedFrom":makeQuery(id+"F3.boolean.opBoolean","COPY",FACE,{"derivedFrom":makeQuery(id+"F3.opExtrude","CAP_FACE",FACE,{"disambiguationData":[OSD([subQ5,subQ1,subQ6,subQ7,subQ4,subQ3,subQ2,subQ0])],"isStart":false})})}),makeQuery(id+"F8.opExtrude","SWEPT_FACE",FACE,{"disambiguationData":[OSD([sQuery(id+"F7.wireOp",EDGE,"E67")])]})]});}
            var Q5;
            Q5=makeQuery(id+"F8.boolean.opBoolean","INTERSECT",EDGE,{"disambiguationData":[OD(0.0)],"derivedFrom":[makeQuery(id+"F5.opExtrude","SWEPT_FACE",FACE,{"disambiguationData":[OSD([sQuery(id+"F4.wireOp",EDGE,"E30")])]}),makeQuery(id+"F8.opExtrude","SWEPT_FACE",FACE,{"disambiguationData":[OSD([sQuery(id+"F7.wireOp",EDGE,"E67")])]})]});
            fillet(context, id + "F14", {"entities" : qUnion([Q0, Q1, Q2, Q3, Q4, Q5]), "radius" : 3 * mm, "tangentPropagation" : true, "allowEdgeOverflow" : false});
        }
        {
            var Q0;
            Q0=makeQuery(id+"F1.opExtrude","CAP_EDGE",EDGE,{"disambiguationData":[OSD([sQuery(id+"F0.wireOp",EDGE,"E1.bottom")])],"isStart":false});
            fillet(context, id + "F15", {"entities" : qUnion([Q0]), "radius" : 2 * mm, "tangentPropagation" : true, "allowEdgeOverflow" : false});
        }
        {
            var Q0;
            {var subQ0=sQuery(id+"F0.wireOp",EDGE,"E21.filletArc");var subQ1=sQuery(id+"F0.wireOp",EDGE,"E7");var subQ2=sQuery(id+"F0.wireOp",EDGE,"E6");var subQ3=sQuery(id+"F0.wireOp",EDGE,"E5");var subQ4=sQuery(id+"F0.wireOp",EDGE,"E4");var subQ5=sQuery(id+"F0.wireOp",EDGE,"E22.filletArc");var subQ6=sQuery(id+"F0.wireOp",EDGE,"E1.bottom");var subQ7=sQuery(id+"F0.wireOp",EDGE,"E1.right");var subQ8=sQuery(id+"F0.wireOp",EDGE,"E1.top");var subQ9=sQuery(id+"F0.wireOp",EDGE,"E1.left");var subQ10=sQuery(id+"F0.wireOp",EDGE,"E23.filletArc");var subQ11=sQuery(id+"F0.wireOp",EDGE,"E24.filletArc");Q0=makeQuery(id+"F2.boolean.opBoolean","SPLIT",FACE,{"disambiguationData":[TD([makeQuery(id+"F1.opExtrude","SWEPT_FACE",FACE,{"disambiguationData":[OSD([subQ6])]})])],"derivedFrom":makeQuery(id+"F1.opExtrude","CAP_FACE",FACE,{"disambiguationData":[OSD([subQ6,subQ8,subQ9,subQ7,subQ4,subQ3,subQ2,subQ1,subQ0,subQ5,subQ10,subQ11])],"isStart":true})});}
            var sketch = newSketch(context, id + "F16", { "sketchPlane" : qUnion([Q0])});
            skLineSegment(sketch, "E79", {"start": v(0, 90) * mm, "end": v(0, 120) * mm, "construction": true});
            skCircle(sketch, "E80", {"center": v(0, 120) * mm, "radius": 6 * mm});
            skLineSegment(sketch, "E81", {"start": v(-33, 90) * mm, "end": v(-15, 108) * mm});
            skLineSegment(sketch, "E82", {"start": v(-15, 108) * mm, "end": v(-15, 120) * mm});
            skArc(sketch, "E83", {"start": v(15, 120) * mm, "mid": v(0, 135) * mm, "end": v(-15, 120) * mm});
            skLineSegment(sketch, "E84", {"start": v(15, 120) * mm, "end": v(15, 108) * mm});
            skLineSegment(sketch, "E85", {"start": v(15, 108) * mm, "end": v(33, 90) * mm});
            skLineSegment(sketch, "E86", {"start": v(-80, 0) * mm, "end": v(80, 0) * mm, "construction": true});
            skLineSegment(sketch, "E87.MirrorCS", {"start": v(-15, -108) * mm, "end": v(-15, -120) * mm});
            skLineSegment(sketch, "E88.MirrorCS", {"start": v(15, -120) * mm, "end": v(15, -108) * mm});
            skLineSegment(sketch, "E89.MirrorCS", {"start": v(0, -90) * mm, "end": v(0, -120) * mm, "construction": true});
            skCircle(sketch, "E90.MirrorC", {"center": v(0, -120) * mm, "radius": 6 * mm});
            skLineSegment(sketch, "E91.MirrorCS", {"start": v(-33, -90) * mm, "end": v(-15, -108) * mm});
            skArc(sketch, "E92.MirrorCS", {"start": v(15, -120) * mm, "mid": v(0, -135) * mm, "end": v(-15, -120) * mm});
            skLineSegment(sketch, "E93.MirrorCS", {"start": v(15, -108) * mm, "end": v(33, -90) * mm});
            skLineSegment(sketch, "E94", {"start": v(-33, 90) * mm, "end": v(33, 90) * mm});
            skLineSegment(sketch, "E95", {"start": v(-33, -90) * mm, "end": v(33, -90) * mm});
            skSolve(sketch);
        }
        {
            var Q0;
            Q0=makeQuery(id+"F16.imprint","IMPRINT",FACE,{"disambiguationData":[TD([[makeQuery(id+"F16.imprint","IMPRINT",EDGE,{"derivedFrom":sQuery(id+"F16.wireOp",EDGE,"E80")}),-1.0]])]});
            var Q1;
            Q1=makeQuery(id+"F16.imprint","IMPRINT",FACE,{"disambiguationData":[TD([[makeQuery(id+"F16.imprint","IMPRINT",EDGE,{"derivedFrom":makeQuery(id+"F1.opExtrude","CAP_EDGE",EDGE,{"disambiguationData":[OSD([sQuery(id+"F0.wireOp",EDGE,"E1.left")])],"isStart":true})}),-1.0]])]});
            var Q2;
            Q2=makeQuery(id+"F16.imprint","IMPRINT",FACE,{"disambiguationData":[TD([[makeQuery(id+"F16.imprint","IMPRINT",EDGE,{"derivedFrom":sQuery(id+"F16.wireOp",EDGE,"E87.MirrorCS")}),1.0]])]});
            var Q3;
            Q3=makeQuery(id+"F2.opExtrude","CAP_FACE",FACE,{"disambiguationData":[OSD([sQuery(id+"F0.wireOp",EDGE,"E12"),sQuery(id+"F0.wireOp",EDGE,"E13"),sQuery(id+"F0.wireOp",EDGE,"E14"),sQuery(id+"F0.wireOp",EDGE,"E15"),sQuery(id+"F0.wireOp",EDGE,"E17.filletArc"),sQuery(id+"F0.wireOp",EDGE,"E18.filletArc"),sQuery(id+"F0.wireOp",EDGE,"E19.filletArc"),sQuery(id+"F0.wireOp",EDGE,"E20.filletArc"),sQuery(id+"F0.wireOp",EDGE,"E25.0"),sQuery(id+"F0.wireOp",EDGE,"E25.1"),sQuery(id+"F0.wireOp",EDGE,"E25.2"),sQuery(id+"F0.wireOp",EDGE,"E25.3"),sQuery(id+"F0.wireOp",EDGE,"E25.4"),sQuery(id+"F0.wireOp",EDGE,"E25.5"),sQuery(id+"F0.wireOp",EDGE,"E25.6"),sQuery(id+"F0.wireOp",EDGE,"E25.7")])],"isStart":false});
            extrude(context, id + "F17", {"entities" : qUnion([Q0, Q1, Q2]), "endBound" : BoundingType.UP_TO_SURFACE, "endBoundEntityFace" : qUnion([Q3]), "depth" : 25 * mm});
        }
    });
